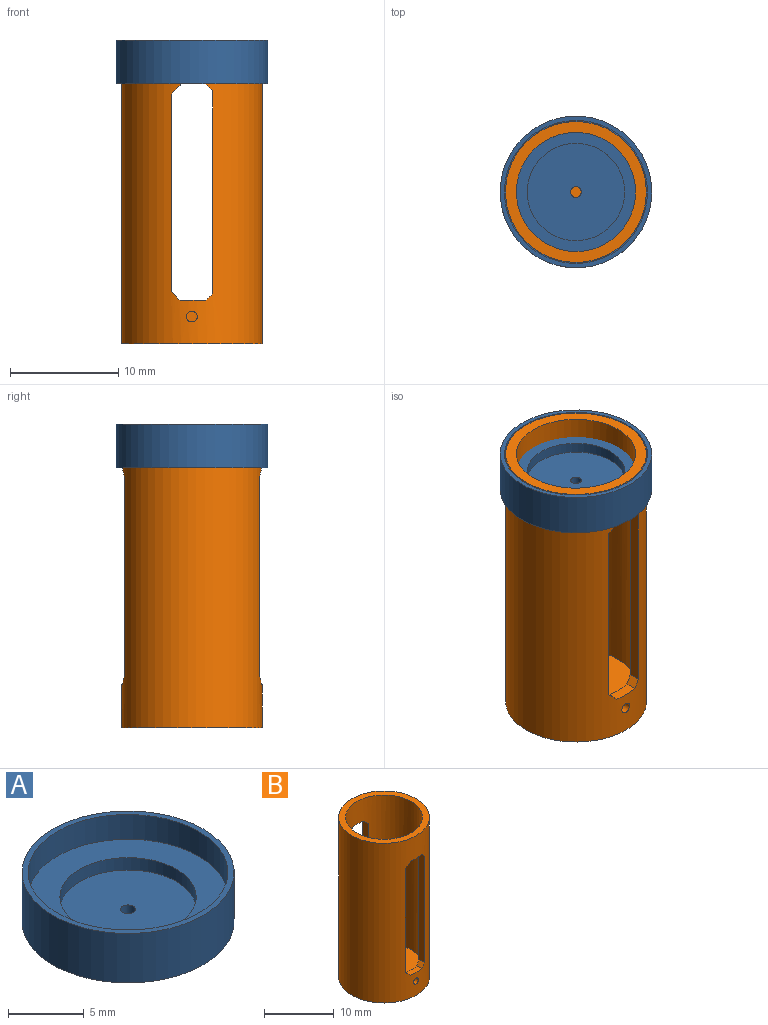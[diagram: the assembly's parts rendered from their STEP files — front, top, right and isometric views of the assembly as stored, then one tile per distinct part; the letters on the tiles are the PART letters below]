
ASSEMBLY  parts=2 mates=1
PART A: 8 faces, bbox 14x14x4 mm
  f0: cylinder r=7mm len=14mm, axis (0,0,-1), area 175.9mm2, adj f1,f2
  f1: plane 14x14mm, normal (0,0,1), area 17.1mm2, adj f0,f3
  f2: plane 14x14mm, normal (0,0,-1), area 153.2mm2, adj f0,f7
  f3: cylinder r=6.6mm len=13.2mm, axis (0,0,-1), area 82.9mm2, adj f1,f4
  f4: plane 13.2x13.2mm, normal (0,0,1), area 73.2mm2, adj f3,f5
  f5: cylinder r=4.5mm len=9mm, axis (0,0,-1), area 28.3mm2, adj f4,f6
  f6: plane 9x9mm, normal (0,0,1), area 62.8mm2, adj f5,f7
  f7: cylinder r=0.5mm len=1mm, axis (0,0,-1), area 3.1mm2, adj f2,f6
PART B: 22 faces, bbox 13x13x28 mm
  f0: cylinder r=6.5mm len=28mm, axis (0,0,-1), area 988.8mm2, adj f2,f3,f5,f6,f7,f8,f9,f10
  f1: cylinder r=5.5mm len=26mm, axis (0,0,-1), area 742.8mm2, adj f2,f4,f5,f6,f7,f8,f9,f10
  f2: plane 13x13mm, normal (0,0,1), area 37.7mm2, adj f0,f1
  f3: plane 13x13mm, normal (0,0,-1), area 132.7mm2, adj f0
  f4: plane 11x11mm, normal (0,0,1), area 95mm2, adj f1
  f5: cylinder r=0.5mm len=1.02mm, axis (0,1,0), area 3.1mm2, adj f0,f1
  f6: plane 18.69x1.06mm, normal (-1,0,0), area 19.7mm2, adj f0,f1,f7,f13
  f7: plane 1.23x0.65mm, normal (-0.71,0,0.71), area 0.9mm2, adj f0,f1,f6,f8
  f8: plane 2.38x1.15mm, normal (0,0,1), area 2.4mm2, adj f0,f1,f7,f9
  f9: plane 1.27x0.84mm, normal (0.71,0,0.71), area 1.2mm2, adj f0,f1,f8,f10
  f10: plane 18.21x1.06mm, normal (1,0,0), area 19.2mm2, adj f0,f1,f9,f11
  f11: plane 1.29x0.97mm, normal (0.71,0,-0.71), area 1.4mm2, adj f0,f1,f10,f12
  f12: plane 2.22x1.15mm, normal (0,0,-1), area 2.2mm2, adj f0,f1,f11,f13
  f13: plane 1.23x0.68mm, normal (-0.71,0,-0.71), area 1mm2, adj f0,f1,f6,f12
  f14: plane 1.23x0.68mm, normal (-0.71,0,-0.71), area 1mm2, adj f0,f1,f15,f21
  f15: plane 2.22x1.15mm, normal (0,0,-1), area 2.2mm2, adj f0,f1,f14,f16
  f16: plane 1.29x0.97mm, normal (0.71,0,-0.71), area 1.4mm2, adj f0,f1,f15,f17
  f17: plane 18.21x1.06mm, normal (1,0,0), area 19.2mm2, adj f0,f1,f16,f18
  f18: plane 1.27x0.84mm, normal (0.71,0,0.71), area 1.2mm2, adj f0,f1,f17,f19
  f19: plane 2.38x1.15mm, normal (0,0,1), area 2.4mm2, adj f0,f1,f18,f20
  f20: plane 1.23x0.65mm, normal (-0.71,0,0.71), area 0.9mm2, adj f0,f1,f19,f21
  f21: plane 18.69x1.06mm, normal (-1,0,0), area 19.7mm2, adj f0,f1,f14,f20
PLACE A rot(axis=(0,1,0),0deg) t=(-17.41,5.3,20.03)mm
PLACE B t=(-2.41,5.3,-3.97)mm fixed
MATE fastened B.f0 <-> A.f3  axis (0,0,1) through (-2.41,5.3,24.03)mm
